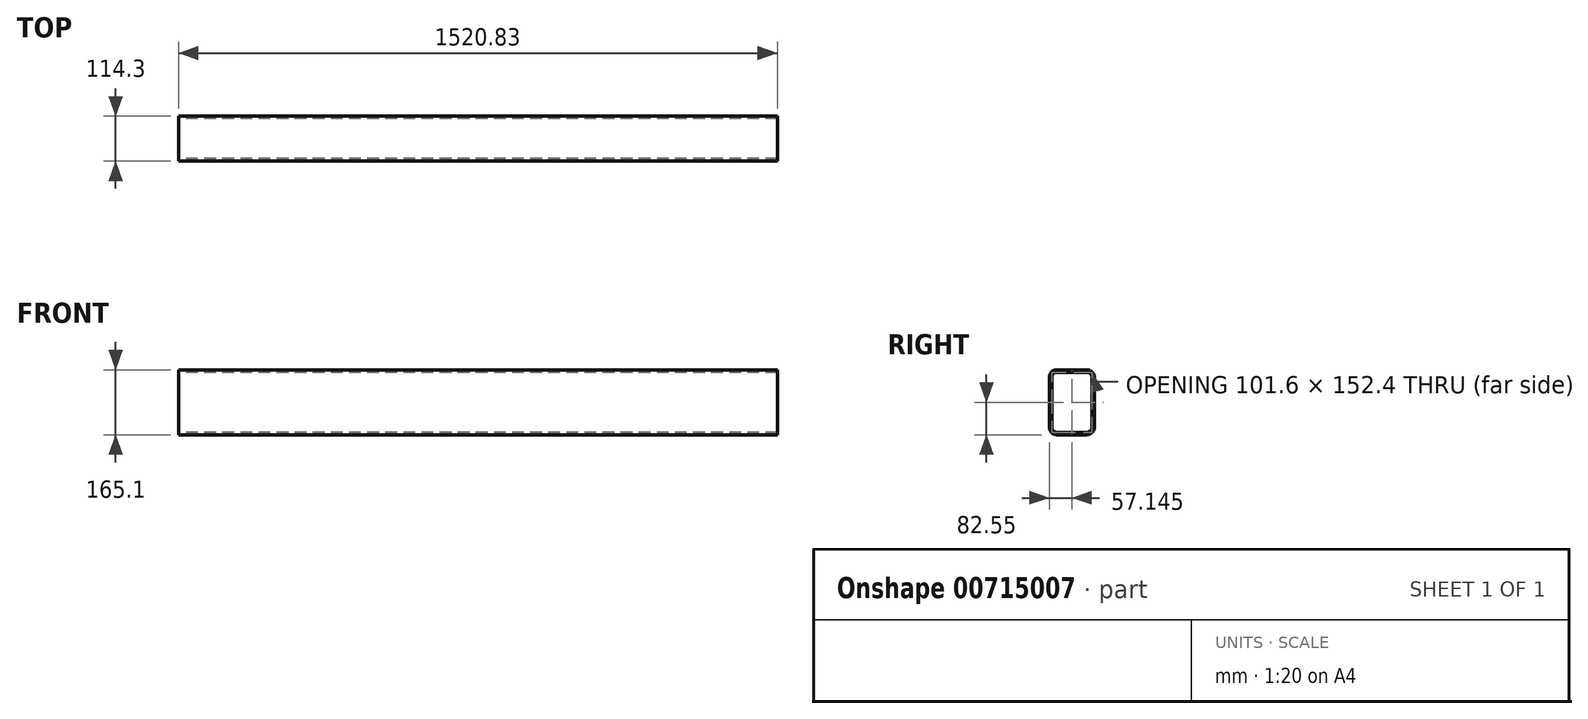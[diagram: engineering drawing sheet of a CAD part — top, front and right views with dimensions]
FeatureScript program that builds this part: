
annotation { "Feature Type Name" : "Feature", "Feature Type Description" : "" }
export const myFeature = defineFeature(function(context is Context, id is Id, definition is map)
    precondition{}
    {
        {
            var Q0;
            Q0=qCreatedBy(makeId("Right.planeOp"),FACE);
            var sketch = newSketch(context, id + "F0", { "sketchPlane" : qUnion([Q0])});
            skLineSegment(sketch, "E0.bottom", {"start": v(14.57, -78.74) * mm, "end": v(-61.63, -78.74) * mm});
            skLineSegment(sketch, "E0.top", {"start": v(14.57, 73.66) * mm, "end": v(-61.63, 73.66) * mm});
            skLineSegment(sketch, "E0.left", {"start": v(27.27, -66.04) * mm, "end": v(27.27, 60.96) * mm});
            skLineSegment(sketch, "E0.right", {"start": v(-74.33, -66.04) * mm, "end": v(-74.33, 60.96) * mm});
            skPoint(sketch, "E0.middle", {"position": v(-23.53, -2.54) * mm});
            skPoint(sketch, "E1.visualSharp", {"position": v(-74.33, 73.66) * mm});
            skArc(sketch, "E1.filletArc", {"start": v(-61.63, 73.66) * mm, "mid": v(-70.62, 69.94) * mm, "end": v(-74.33, 60.96) * mm});
            skPoint(sketch, "E2.visualSharp", {"position": v(27.27, 73.66) * mm});
            skArc(sketch, "E2.filletArc", {"start": v(27.27, 60.96) * mm, "mid": v(23.55, 69.94) * mm, "end": v(14.57, 73.66) * mm});
            skPoint(sketch, "E3.visualSharp", {"position": v(27.27, -78.74) * mm});
            skArc(sketch, "E3.filletArc", {"start": v(14.57, -78.74) * mm, "mid": v(23.55, -75.02) * mm, "end": v(27.27, -66.04) * mm});
            skPoint(sketch, "E4.visualSharp", {"position": v(-74.33, -78.74) * mm});
            skArc(sketch, "E4.filletArc", {"start": v(-74.33, -66.04) * mm, "mid": v(-70.62, -75.02) * mm, "end": v(-61.63, -78.74) * mm});
            skLineSegment(sketch, "E5.0", {"start": v(33.62, -66.04) * mm, "end": v(33.62, 60.96) * mm});
            skArc(sketch, "E5.1", {"start": v(14.57, -85.09) * mm, "mid": v(28.04, -79.51) * mm, "end": v(33.62, -66.04) * mm});
            skArc(sketch, "E5.2", {"start": v(33.62, 60.96) * mm, "mid": v(28.04, 74.43) * mm, "end": v(14.57, 80.01) * mm});
            skLineSegment(sketch, "E5.3", {"start": v(14.57, -85.09) * mm, "end": v(-61.63, -85.09) * mm});
            skLineSegment(sketch, "E5.4", {"start": v(14.57, 80.01) * mm, "end": v(-61.63, 80.01) * mm});
            skArc(sketch, "E5.5", {"start": v(-61.63, 80.01) * mm, "mid": v(-75.1, 74.43) * mm, "end": v(-80.68, 60.96) * mm});
            skLineSegment(sketch, "E5.6", {"start": v(-80.68, -66.04) * mm, "end": v(-80.68, 60.96) * mm});
            skArc(sketch, "E5.7", {"start": v(-80.68, -66.04) * mm, "mid": v(-75.1, -79.51) * mm, "end": v(-61.63, -85.09) * mm});
            skSolve(sketch);
        }
        {
            var Q0;
            Q0=makeQuery(id+"F0.imprint","IMPRINT",FACE,{"disambiguationData":[TD([[makeQuery(id+"F0.imprint","IMPRINT",EDGE,{"derivedFrom":sQuery(id+"F0.wireOp",EDGE,"E0.bottom")}),1.0]])]});
            extrude(context, id + "F1", {"entities" : qUnion([Q0]), "depth" : 1520.82 * mm, "offsetDistance" : 25.4 * mm});
        }
    });
